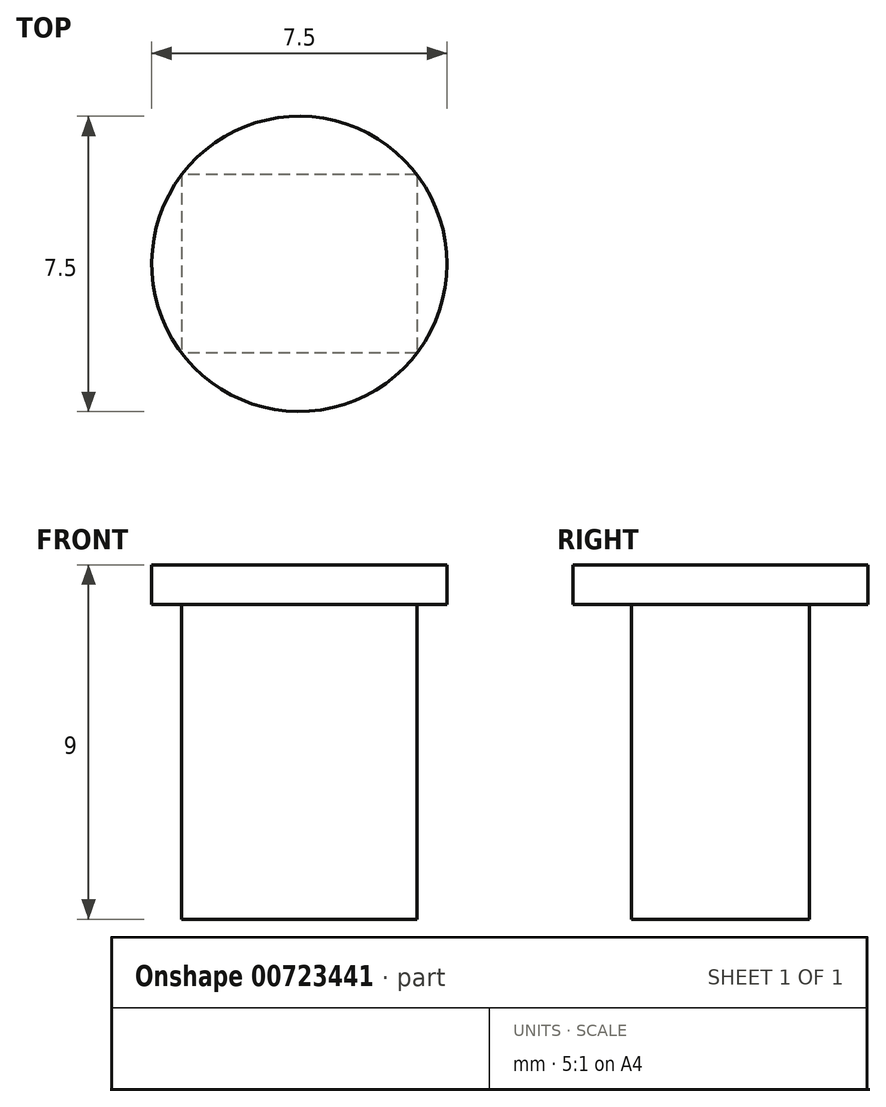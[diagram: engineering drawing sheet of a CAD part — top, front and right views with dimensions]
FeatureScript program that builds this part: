
annotation { "Feature Type Name" : "Feature", "Feature Type Description" : "" }
export const myFeature = defineFeature(function(context is Context, id is Id, definition is map)
    precondition{}
    {
        {
            var Q0;
            Q0=qCreatedBy(makeId("Top.planeOp"),FACE);
            var sketch = newSketch(context, id + "F0", { "sketchPlane" : qUnion([Q0])});
            skCircle(sketch, "E0", {"center": v(0, 0) * mm, "radius": 3.6 * mm});
            skCircle(sketch, "E1", {"center": v(0, 0) * mm, "radius": 3.75 * mm});
            skSolve(sketch);
        }
        {
            var Q0;
            Q0=sQuery(id+"F0.wireOp",EDGE,"E1");
            extrude(context, id + "F1", {"bodyType" : ToolBodyType.SURFACE, "surfaceEntities" : qUnion([Q0]), "depth" : 20.6 * mm, "offsetDistance" : 25 * mm});
        }
        {
            var Q0;
            Q0=qCreatedBy(makeId("Top.planeOp"),FACE);
            var sketch = newSketch(context, id + "F2", { "sketchPlane" : qUnion([Q0])});
            skCircle(sketch, "E2", {"center": v(0, 0) * mm, "radius": 3.75 * mm});
            skSolve(sketch);
        }
        {
            var Q0;
            Q0=makeQuery(id+"F2.imprint","IMPRINT",FACE,{"disambiguationData":[TD([[makeQuery(id+"F2.imprint","IMPRINT",EDGE,{"derivedFrom":sQuery(id+"F2.wireOp",EDGE,"E2")}),1.0]])]});
            extrude(context, id + "F3", {"entities" : qUnion([Q0]), "depth" : 1 * mm, "offsetDistance" : 25 * mm});
        }
        {
            var Q0;
            Q0=makeQuery(id+"F3.opExtrude","CAP_FACE",FACE,{"disambiguationData":[OSD([sQuery(id+"F2.wireOp",EDGE,"E2")])],"isStart":true});
            var sketch = newSketch(context, id + "F4", { "sketchPlane" : qUnion([Q0])});
            skLineSegment(sketch, "E3.bottom", {"start": v(2.99, -2.26) * mm, "end": v(-2.99, -2.26) * mm});
            skLineSegment(sketch, "E3.top", {"start": v(2.99, 2.26) * mm, "end": v(-2.99, 2.26) * mm});
            skLineSegment(sketch, "E3.left", {"start": v(2.99, -2.26) * mm, "end": v(2.99, 2.26) * mm});
            skLineSegment(sketch, "E3.right", {"start": v(-2.99, -2.26) * mm, "end": v(-2.99, 2.26) * mm});
            skPoint(sketch, "E3.middle", {"position": v(0, 0) * mm});
            skSolve(sketch);
        }
        {
            var Q0;
            Q0=makeQuery(id+"F4.imprint","IMPRINT",FACE,{"disambiguationData":[TD([[makeQuery(id+"F4.imprint","IMPRINT",EDGE,{"derivedFrom":sQuery(id+"F4.wireOp",EDGE,"E3.bottom")}),-1.0]])]});
            extrude(context, id + "F5", {"entities" : qUnion([Q0]), "operationType" : NewBodyOperationType.ADD, "depth" : 3 * mm, "offsetDistance" : 25 * mm});
        }
        {
            var Q0;
            Q0=makeQuery(id+"F5.opExtrude","CAP_FACE",FACE,{"disambiguationData":[OSD([sQuery(id+"F4.wireOp",EDGE,"E3.bottom"),sQuery(id+"F4.wireOp",EDGE,"E3.top"),sQuery(id+"F4.wireOp",EDGE,"E3.left"),sQuery(id+"F4.wireOp",EDGE,"E3.right")])],"isStart":false});
            extrude(context, id + "F6", {"entities" : qUnion([Q0]), "operationType" : NewBodyOperationType.ADD, "depth" : 5 * mm, "offsetDistance" : 25 * mm});
        }
        {
            var Q0;
            {var subQ0=sQuery(id+"F4.wireOp",EDGE,"E3.bottom");Q0=makeQuery(id+"F6.boolean.opBoolean","MERGE",FACE,{"derivedFrom":[makeQuery(id+"F5.opExtrude","SWEPT_FACE",FACE,{"disambiguationData":[OSD([subQ0])]}),makeQuery(id+"F6.opExtrude","SWEPT_FACE",FACE,{"disambiguationData":[OSD([subQ0])]})]});}
            var sketch = newSketch(context, id + "F7", { "sketchPlane" : qUnion([Q0])});
            skCircle(sketch, "E4", {"center": v(0, -3.82) * mm, "radius": 3.65 * mm});
            skSolve(sketch);
        }
        {
            var Q0;
            Q0=sQuery(id+"F7.wireOp",EDGE,"E4");
            extrude(context, id + "F8", {"bodyType" : ToolBodyType.SURFACE, "surfaceEntities" : qUnion([Q0]), "depth" : 20 * mm, "offsetDistance" : 25 * mm});
        }
    });
